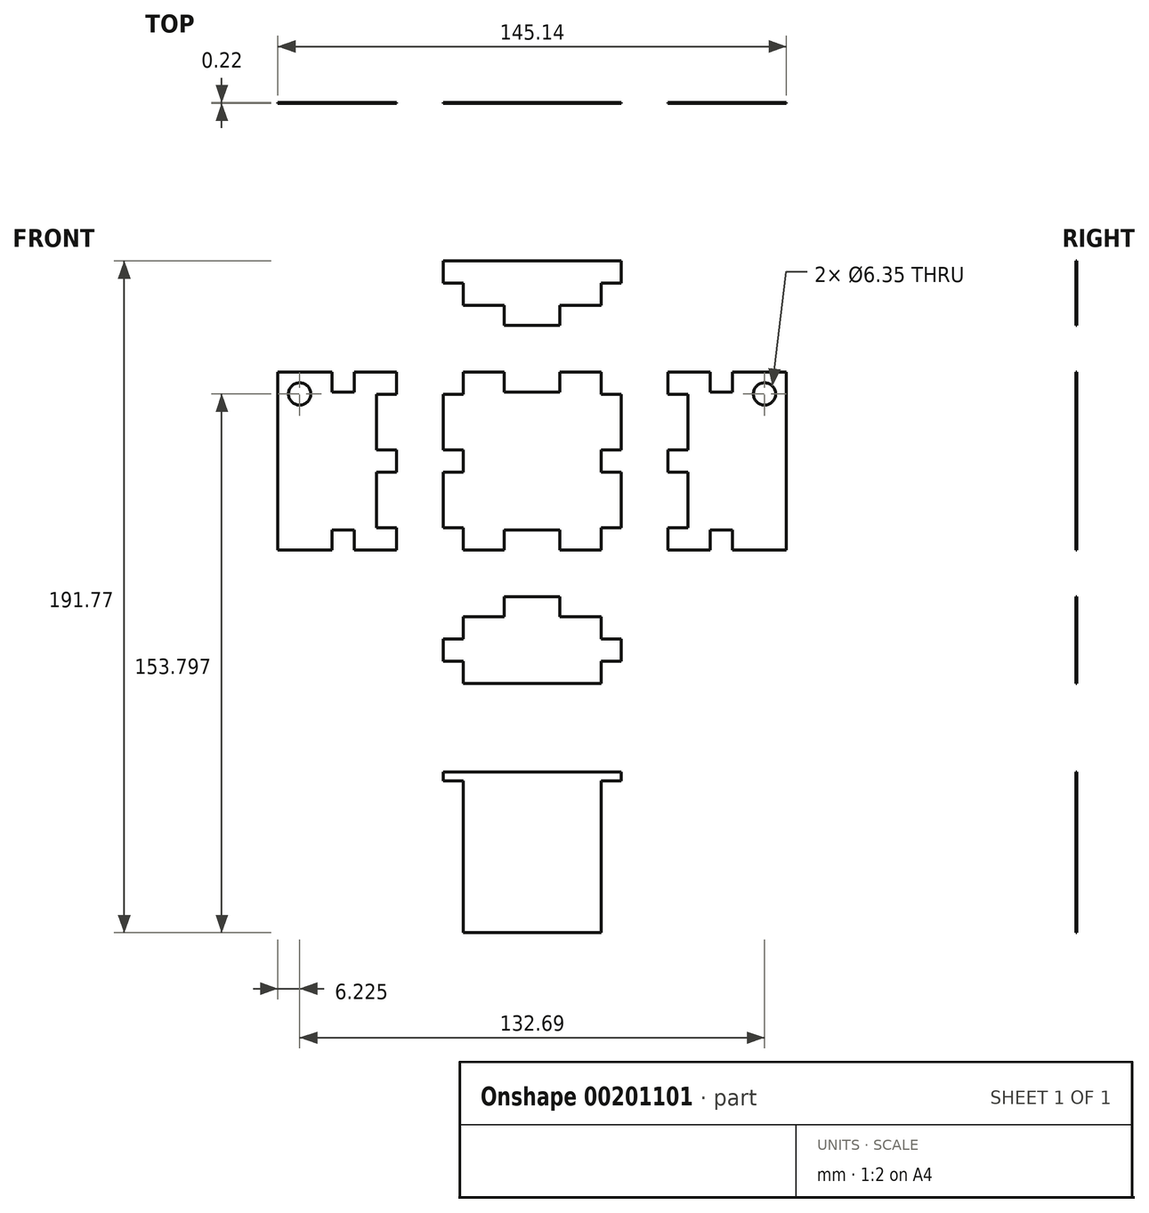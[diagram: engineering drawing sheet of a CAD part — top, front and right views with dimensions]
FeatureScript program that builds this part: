
annotation { "Feature Type Name" : "Feature", "Feature Type Description" : "" }
export const myFeature = defineFeature(function(context is Context, id is Id, definition is map)
    precondition{}
    {
        {
            assignVariable(context, id + "F0", {"name" : "thick", "anyValue" : .224});
        }
        {
            var Q0;
            Q0=qCreatedBy(makeId("Front.planeOp"),FACE);
            var sketch = newSketch(context, id + "F1", { "sketchPlane" : qUnion([Q0])});
            skLineSegment(sketch, "E0.bottom", {"start": v(-19.71, 25.4) * mm, "end": v(-7.94, 25.4) * mm});
            skLineSegment(sketch, "E0.top", {"start": v(-19.71, -25.4) * mm, "end": v(-7.94, -25.4) * mm});
            skLineSegment(sketch, "E0.left", {"start": v(-25.4, 19.05) * mm, "end": v(-25.4, 3.17) * mm});
            skLineSegment(sketch, "E0.right", {"start": v(25.4, 19.05) * mm, "end": v(25.4, 3.17) * mm});
            skPoint(sketch, "E0.middle", {"position": v(0, 0) * mm});
            skLineSegment(sketch, "E1.bottom", {"start": v(-44.45, 25.4) * mm, "end": v(-50.8, 25.4) * mm});
            skLineSegment(sketch, "E1.top", {"start": v(-44.45, -25.4) * mm, "end": v(-50.8, -25.4) * mm});
            skLineSegment(sketch, "E1.left", {"start": v(-44.45, 19.05) * mm, "end": v(-44.45, 3.17) * mm});
            skLineSegment(sketch, "E1.right", {"start": v(-63.5, 12.95) * mm, "end": v(-63.5, -25.4) * mm});
            skLineSegment(sketch, "E2.bottom", {"start": v(25.4, 44.45) * mm, "end": v(7.94, 44.45) * mm});
            skLineSegment(sketch, "E2.top", {"start": v(25.4, 57.15) * mm, "end": v(-25.4, 57.15) * mm});
            skLineSegment(sketch, "E2.left", {"start": v(25.4, 44.45) * mm, "end": v(25.4, 57.15) * mm, "construction": true});
            skLineSegment(sketch, "E2.right", {"start": v(-25.4, 44.45) * mm, "end": v(-25.4, 57.15) * mm, "construction": true});
            skCircle(sketch, "E3", {"center": v(-66.34, 19.18) * mm, "radius": 3.18 * mm});
            skArc(sketch, "E4", {"start": v(-66.34, 25.4) * mm, "mid": v(-72.57, 19.18) * mm, "end": v(-66.34, 12.95) * mm});
            skLineSegment(sketch, "E5", {"start": v(-63.5, 25.4) * mm, "end": v(-66.34, 25.4) * mm});
            skLineSegment(sketch, "E6", {"start": v(-66.34, 12.95) * mm, "end": v(-63.5, 12.95) * mm});
            skLineSegment(sketch, "E7", {"start": v(0, 25.4) * mm, "end": v(0, -25.4) * mm, "construction": true});
            skLineSegment(sketch, "E8.MirrorCS", {"start": v(63.5, 25.4) * mm, "end": v(66.34, 25.4) * mm});
            skCircle(sketch, "E9.MirrorC", {"center": v(66.34, 19.18) * mm, "radius": 3.18 * mm});
            skLineSegment(sketch, "E10.MirrorCS", {"start": v(66.34, 12.95) * mm, "end": v(63.5, 12.95) * mm});
            skLineSegment(sketch, "E11.MirrorCS", {"start": v(63.5, 12.95) * mm, "end": v(63.5, -25.4) * mm});
            skLineSegment(sketch, "E12.MirrorCS", {"start": v(44.45, 19.05) * mm, "end": v(44.45, 3.17) * mm});
            skLineSegment(sketch, "E13.MirrorCS", {"start": v(44.45, -25.4) * mm, "end": v(50.8, -25.4) * mm});
            skLineSegment(sketch, "E14.MirrorCS", {"start": v(44.45, 25.4) * mm, "end": v(63.5, 25.4) * mm});
            skArc(sketch, "E15.MirrorCS", {"start": v(66.34, 25.4) * mm, "mid": v(72.57, 19.18) * mm, "end": v(66.34, 12.95) * mm});
            skLineSegment(sketch, "E16.bottom", {"start": v(-25.4, -44.45) * mm, "end": v(-7.94, -44.45) * mm});
            skLineSegment(sketch, "E16.top", {"start": v(-25.4, -63.5) * mm, "end": v(25.4, -63.5) * mm});
            skLineSegment(sketch, "E16.left", {"start": v(-25.4, -44.45) * mm, "end": v(-25.4, -63.5) * mm, "construction": true});
            skLineSegment(sketch, "E16.right", {"start": v(25.4, -44.45) * mm, "end": v(25.4, -63.5) * mm, "construction": true});
            skLineSegment(sketch, "E17.bottom", {"start": v(-19.71, -82.55) * mm, "end": v(19.71, -82.55) * mm});
            skLineSegment(sketch, "E17.top", {"start": v(-19.71, -92.71) * mm, "end": v(19.71, -92.71) * mm, "construction": true});
            skLineSegment(sketch, "E17.left", {"start": v(-19.71, -82.55) * mm, "end": v(-19.71, -88.77) * mm});
            skLineSegment(sketch, "E17.right", {"start": v(19.71, -82.55) * mm, "end": v(19.71, -88.77) * mm});
            skLineSegment(sketch, "E18", {"start": v(-19.71, 25.4) * mm, "end": v(-19.71, 19.05) * mm});
            skLineSegment(sketch, "E19", {"start": v(-19.71, 19.05) * mm, "end": v(-25.4, 19.05) * mm});
            skLineSegment(sketch, "E20", {"start": v(-25.4, 3.17) * mm, "end": v(-19.71, 3.17) * mm});
            skLineSegment(sketch, "E21", {"start": v(-19.71, 3.17) * mm, "end": v(-19.71, -3.18) * mm});
            skLineSegment(sketch, "E22", {"start": v(-19.71, -3.18) * mm, "end": v(-25.4, -3.18) * mm});
            skLineSegment(sketch, "E23", {"start": v(-25.4, -19.05) * mm, "end": v(-19.71, -19.05) * mm});
            skLineSegment(sketch, "E24", {"start": v(-19.71, -19.05) * mm, "end": v(-19.71, -25.4) * mm});
            skLineSegment(sketch, "E25", {"start": v(-44.45, 25.4) * mm, "end": v(-38.76, 25.4) * mm});
            skLineSegment(sketch, "E26", {"start": v(-38.76, 25.4) * mm, "end": v(-38.76, 19.05) * mm});
            skLineSegment(sketch, "E27", {"start": v(-38.76, 19.05) * mm, "end": v(-44.45, 19.05) * mm});
            skLineSegment(sketch, "E28", {"start": v(-44.45, 3.17) * mm, "end": v(-38.76, 3.17) * mm});
            skLineSegment(sketch, "E29", {"start": v(-38.76, 3.17) * mm, "end": v(-38.76, -3.18) * mm});
            skLineSegment(sketch, "E30", {"start": v(-38.76, -3.18) * mm, "end": v(-44.45, -3.18) * mm});
            skLineSegment(sketch, "E31", {"start": v(-44.45, -19.05) * mm, "end": v(-38.76, -19.05) * mm});
            skLineSegment(sketch, "E32", {"start": v(-38.76, -19.05) * mm, "end": v(-38.76, -25.4) * mm});
            skLineSegment(sketch, "E33", {"start": v(-38.76, -25.4) * mm, "end": v(-44.45, -25.4) * mm});
            skLineSegment(sketch, "E34.MirrorCS", {"start": v(38.76, 19.05) * mm, "end": v(44.45, 19.05) * mm});
            skLineSegment(sketch, "E35.MirrorCS", {"start": v(38.76, 25.4) * mm, "end": v(38.76, 19.05) * mm});
            skLineSegment(sketch, "E36.MirrorCS", {"start": v(44.45, 3.17) * mm, "end": v(38.76, 3.17) * mm});
            skLineSegment(sketch, "E37.MirrorCS", {"start": v(44.45, 25.4) * mm, "end": v(38.76, 25.4) * mm});
            skLineSegment(sketch, "E38.MirrorCS", {"start": v(38.76, 3.17) * mm, "end": v(38.76, -3.18) * mm});
            skLineSegment(sketch, "E39.MirrorCS", {"start": v(38.76, -3.18) * mm, "end": v(44.45, -3.18) * mm});
            skLineSegment(sketch, "E40.MirrorCS", {"start": v(38.76, -19.05) * mm, "end": v(38.76, -25.4) * mm});
            skLineSegment(sketch, "E41.MirrorCS", {"start": v(38.76, -25.4) * mm, "end": v(44.45, -25.4) * mm});
            skLineSegment(sketch, "E42.MirrorCS", {"start": v(44.45, -19.05) * mm, "end": v(38.76, -19.05) * mm});
            skLineSegment(sketch, "E43.MirrorCS", {"start": v(19.71, 19.05) * mm, "end": v(25.4, 19.05) * mm});
            skLineSegment(sketch, "E44.MirrorCS", {"start": v(19.71, 25.4) * mm, "end": v(19.71, 19.05) * mm});
            skLineSegment(sketch, "E45.MirrorCS", {"start": v(25.4, 3.17) * mm, "end": v(19.71, 3.17) * mm});
            skLineSegment(sketch, "E46.MirrorCS", {"start": v(19.71, 3.17) * mm, "end": v(19.71, -3.18) * mm});
            skLineSegment(sketch, "E47.MirrorCS", {"start": v(19.71, -3.18) * mm, "end": v(25.4, -3.18) * mm});
            skLineSegment(sketch, "E48.MirrorCS", {"start": v(25.4, -19.05) * mm, "end": v(19.71, -19.05) * mm});
            skLineSegment(sketch, "E49.MirrorCS", {"start": v(19.71, -19.05) * mm, "end": v(19.71, -25.4) * mm});
            skLineSegment(sketch, "E50", {"start": v(-7.94, 25.4) * mm, "end": v(-7.94, 19.71) * mm});
            skLineSegment(sketch, "E51", {"start": v(-7.94, 19.71) * mm, "end": v(7.94, 19.71) * mm});
            skLineSegment(sketch, "E52", {"start": v(7.94, 19.71) * mm, "end": v(7.94, 25.4) * mm});
            skPoint(sketch, "E53", {"position": v(0, 19.71) * mm});
            skLineSegment(sketch, "E54", {"start": v(-25.4, 0) * mm, "end": v(25.4, 0) * mm, "construction": true});
            skLineSegment(sketch, "E55.MirrorCS", {"start": v(7.94, -19.71) * mm, "end": v(7.94, -25.4) * mm});
            skLineSegment(sketch, "E56.MirrorCS", {"start": v(-7.94, -19.71) * mm, "end": v(7.94, -19.71) * mm});
            skLineSegment(sketch, "E57.MirrorCS", {"start": v(-7.94, -25.4) * mm, "end": v(-7.94, -19.71) * mm});
            skPoint(sketch, "E58.MirrorP", {"position": v(0, -19.71) * mm});
            skLineSegment(sketch, "E59", {"start": v(-53.97, 25.4) * mm, "end": v(-53.97, 19.71) * mm, "construction": true});
            skLineSegment(sketch, "E60", {"start": v(-53.97, 19.71) * mm, "end": v(-57.15, 19.71) * mm, "construction": true});
            skLineSegment(sketch, "E61", {"start": v(-57.15, 19.71) * mm, "end": v(-57.15, 25.4) * mm});
            skLineSegment(sketch, "E62", {"start": v(-57.15, 19.71) * mm, "end": v(-50.8, 19.71) * mm});
            skLineSegment(sketch, "E63", {"start": v(-50.8, 19.71) * mm, "end": v(-50.8, 25.4) * mm});
            skLineSegment(sketch, "E64", {"start": v(-25.4, 50.8) * mm, "end": v(-31.09, 50.8) * mm, "construction": true});
            skPoint(sketch, "E64.endSnap0", {"position": v(-25.4, 50.8) * mm});
            skLineSegment(sketch, "E65", {"start": v(-31.09, 50.8) * mm, "end": v(-31.09, 57.15) * mm, "construction": true});
            skLineSegment(sketch, "E66", {"start": v(-31.09, 57.15) * mm, "end": v(-25.4, 57.15) * mm, "construction": true});
            skLineSegment(sketch, "E67.MirrorCS", {"start": v(53.97, 19.71) * mm, "end": v(57.15, 19.71) * mm, "construction": true});
            skLineSegment(sketch, "E68.MirrorCS", {"start": v(57.15, 19.71) * mm, "end": v(50.8, 19.71) * mm});
            skLineSegment(sketch, "E69.MirrorCS", {"start": v(57.15, 19.71) * mm, "end": v(57.15, 25.4) * mm});
            skLineSegment(sketch, "E70.MirrorCS", {"start": v(53.97, 25.4) * mm, "end": v(53.97, 19.71) * mm, "construction": true});
            skLineSegment(sketch, "E71.MirrorCS", {"start": v(50.8, 19.71) * mm, "end": v(50.8, 25.4) * mm});
            skPoint(sketch, "E72.MirrorP", {"position": v(25.4, 50.8) * mm});
            skLineSegment(sketch, "E73.MirrorCS", {"start": v(31.09, 57.15) * mm, "end": v(25.4, 57.15) * mm, "construction": true});
            skLineSegment(sketch, "E74.MirrorCS", {"start": v(25.4, 50.8) * mm, "end": v(31.09, 50.8) * mm, "construction": true});
            skLineSegment(sketch, "E75.MirrorCS", {"start": v(31.09, 50.8) * mm, "end": v(31.09, 57.15) * mm, "construction": true});
            skPoint(sketch, "E76.MirrorP", {"position": v(-25.4, -50.8) * mm});
            skLineSegment(sketch, "E77.MirrorCS", {"start": v(-25.4, -50.8) * mm, "end": v(-31.09, -50.8) * mm, "construction": true});
            skLineSegment(sketch, "E78.MirrorCS", {"start": v(-31.09, -57.15) * mm, "end": v(-25.4, -57.15) * mm, "construction": true});
            skLineSegment(sketch, "E79.MirrorCS", {"start": v(-31.09, -50.8) * mm, "end": v(-31.09, -57.15) * mm, "construction": true});
            skPoint(sketch, "E80.MirrorP", {"position": v(25.4, -50.8) * mm});
            skLineSegment(sketch, "E81.MirrorCS", {"start": v(25.4, -50.8) * mm, "end": v(31.09, -50.8) * mm, "construction": true});
            skLineSegment(sketch, "E82.MirrorCS", {"start": v(31.09, -50.8) * mm, "end": v(31.09, -57.15) * mm, "construction": true});
            skLineSegment(sketch, "E83.MirrorCS", {"start": v(31.09, -57.15) * mm, "end": v(25.4, -57.15) * mm, "construction": true});
            skLineSegment(sketch, "E84.MirrorCS", {"start": v(50.8, -19.71) * mm, "end": v(50.8, -25.4) * mm});
            skLineSegment(sketch, "E85.MirrorCS", {"start": v(57.15, -19.71) * mm, "end": v(50.8, -19.71) * mm});
            skLineSegment(sketch, "E86.MirrorCS", {"start": v(57.15, -19.71) * mm, "end": v(57.15, -25.4) * mm});
            skLineSegment(sketch, "E87.MirrorCS", {"start": v(-57.15, -19.71) * mm, "end": v(-57.15, -25.4) * mm});
            skLineSegment(sketch, "E88.MirrorCS", {"start": v(-57.15, -19.71) * mm, "end": v(-50.8, -19.71) * mm});
            skLineSegment(sketch, "E89.MirrorCS", {"start": v(-50.8, -19.71) * mm, "end": v(-50.8, -25.4) * mm});
            skLineSegment(sketch, "E90", {"start": v(-25.4, -102.87) * mm, "end": v(-25.4, -134.62) * mm});
            skLineSegment(sketch, "E91", {"start": v(-25.4, -134.62) * mm, "end": v(25.4, -134.62) * mm});
            skLineSegment(sketch, "E92", {"start": v(25.4, -134.62) * mm, "end": v(25.4, -102.87) * mm});
            skLineSegment(sketch, "E93", {"start": v(-19.71, -88.77) * mm, "end": v(-25.4, -88.77) * mm});
            skLineSegment(sketch, "E94", {"start": v(-25.4, -88.77) * mm, "end": v(-25.4, -91.31) * mm});
            skLineSegment(sketch, "E95", {"start": v(-25.4, -91.31) * mm, "end": v(-19.71, -91.31) * mm});
            skLineSegment(sketch, "E96", {"start": v(-19.71, -92.71) * mm, "end": v(-19.71, -96.77) * mm});
            skLineSegment(sketch, "E97", {"start": v(-19.71, -96.77) * mm, "end": v(-25.4, -102.87) * mm});
            skLineSegment(sketch, "E98.MirrorCS", {"start": v(19.71, -92.71) * mm, "end": v(19.71, -96.77) * mm});
            skLineSegment(sketch, "E99.MirrorCS", {"start": v(19.71, -96.77) * mm, "end": v(25.4, -102.87) * mm});
            skLineSegment(sketch, "E100.MirrorCS", {"start": v(25.4, -88.77) * mm, "end": v(25.4, -91.31) * mm});
            skLineSegment(sketch, "E101.MirrorCS", {"start": v(25.4, -91.31) * mm, "end": v(19.71, -91.31) * mm});
            skLineSegment(sketch, "E102.MirrorCS", {"start": v(19.71, -88.77) * mm, "end": v(25.4, -88.77) * mm});
            skLineSegment(sketch, "E103", {"start": v(-7.94, 44.45) * mm, "end": v(-7.94, 38.76) * mm});
            skLineSegment(sketch, "E104", {"start": v(-7.94, 38.76) * mm, "end": v(7.94, 38.76) * mm});
            skLineSegment(sketch, "E105", {"start": v(7.94, 38.76) * mm, "end": v(7.94, 44.45) * mm});
            skLineSegment(sketch, "E106", {"start": v(-7.94, -44.45) * mm, "end": v(-7.94, -38.76) * mm});
            skLineSegment(sketch, "E107", {"start": v(-7.94, -38.76) * mm, "end": v(7.94, -38.76) * mm});
            skLineSegment(sketch, "E108", {"start": v(7.94, -38.76) * mm, "end": v(7.94, -44.45) * mm});
            skLineSegment(sketch, "E109", {"start": v(-19.71, 44.45) * mm, "end": v(-19.71, 50.8) * mm});
            skLineSegment(sketch, "E110", {"start": v(19.71, 44.45) * mm, "end": v(19.71, 50.8) * mm});
            skLineSegment(sketch, "E111", {"start": v(-19.71, 50.8) * mm, "end": v(-25.4, 50.8) * mm});
            skLineSegment(sketch, "E112", {"start": v(-25.4, 50.8) * mm, "end": v(-25.4, 57.15) * mm});
            skLineSegment(sketch, "E113", {"start": v(25.4, 57.15) * mm, "end": v(25.4, 50.8) * mm});
            skLineSegment(sketch, "E114", {"start": v(19.71, 50.8) * mm, "end": v(25.4, 50.8) * mm});
            skLineSegment(sketch, "E115", {"start": v(-19.71, -44.45) * mm, "end": v(-19.71, -50.8) * mm});
            skLineSegment(sketch, "E116", {"start": v(19.71, -44.45) * mm, "end": v(19.71, -50.8) * mm});
            skLineSegment(sketch, "E117", {"start": v(-19.71, -50.8) * mm, "end": v(-25.4, -50.8) * mm});
            skLineSegment(sketch, "E118", {"start": v(-25.4, -57.15) * mm, "end": v(-25.4, -50.8) * mm});
            skLineSegment(sketch, "E119", {"start": v(-25.4, -57.15) * mm, "end": v(-19.71, -57.15) * mm});
            skLineSegment(sketch, "E120", {"start": v(25.4, -50.8) * mm, "end": v(19.71, -50.8) * mm});
            skLineSegment(sketch, "E121", {"start": v(25.4, -50.8) * mm, "end": v(25.4, -57.15) * mm});
            skLineSegment(sketch, "E122", {"start": v(25.4, -57.15) * mm, "end": v(19.71, -57.15) * mm});
            skPoint(sketch, "E123", {"position": v(25.4, -90.04) * mm});
            skPoint(sketch, "E124.orphan", {"position": v(-19.71, 57.15) * mm});
            skLineSegment(sketch, "E125.trimOffspring", {"start": v(-7.94, 44.45) * mm, "end": v(-25.4, 44.45) * mm});
            skPoint(sketch, "E126.orphan", {"position": v(19.71, 57.15) * mm});
            skLineSegment(sketch, "E127.trimOffspring", {"start": v(44.45, -3.18) * mm, "end": v(44.45, -19.05) * mm});
            skLineSegment(sketch, "E128.trimOffspring", {"start": v(57.15, -25.4) * mm, "end": v(63.5, -25.4) * mm});
            skPoint(sketch, "E129.orphan", {"position": v(25.4, -25.4) * mm});
            skLineSegment(sketch, "E130.trimOffspring", {"start": v(25.4, -3.18) * mm, "end": v(25.4, -19.05) * mm});
            skPoint(sketch, "E131.orphan", {"position": v(25.4, 25.4) * mm});
            skLineSegment(sketch, "E132.trimOffspring", {"start": v(7.94, 25.4) * mm, "end": v(19.71, 25.4) * mm});
            skPoint(sketch, "E133.orphan", {"position": v(-25.4, 25.4) * mm});
            skLineSegment(sketch, "E134.trimOffspring", {"start": v(-53.97, 25.4) * mm, "end": v(-63.5, 25.4) * mm});
            skLineSegment(sketch, "E135.trimOffspring", {"start": v(-44.45, -3.18) * mm, "end": v(-44.45, -19.05) * mm});
            skLineSegment(sketch, "E136.trimOffspring", {"start": v(-25.4, -3.18) * mm, "end": v(-25.4, -19.05) * mm});
            skLineSegment(sketch, "E137.trimOffspring", {"start": v(-57.15, -25.4) * mm, "end": v(-63.5, -25.4) * mm});
            skPoint(sketch, "E138.orphan", {"position": v(-25.4, -25.4) * mm});
            skLineSegment(sketch, "E139.trimOffspring", {"start": v(7.94, -25.4) * mm, "end": v(19.71, -25.4) * mm});
            skLineSegment(sketch, "E140.trimOffspring", {"start": v(19.71, -57.15) * mm, "end": v(19.71, -63.5) * mm});
            skLineSegment(sketch, "E141.trimOffspring", {"start": v(7.94, -44.45) * mm, "end": v(25.4, -44.45) * mm});
            skLineSegment(sketch, "E142.trimOffspring", {"start": v(-19.71, -57.15) * mm, "end": v(-19.71, -63.5) * mm});
            skLineSegment(sketch, "E143.trimOffspring", {"start": v(19.71, -91.31) * mm, "end": v(19.71, -92.71) * mm});
            skLineSegment(sketch, "E144.trimOffspring", {"start": v(-19.71, -91.31) * mm, "end": v(-19.71, -92.71) * mm});
            skLineSegment(sketch, "E145.bottom", {"start": v(-75.63, 66.18) * mm, "end": v(74.77, 66.18) * mm});
            skLineSegment(sketch, "E145.top", {"start": v(-75.63, -141.7) * mm, "end": v(74.77, -141.7) * mm});
            skLineSegment(sketch, "E145.left", {"start": v(-75.63, 66.18) * mm, "end": v(-75.63, -141.7) * mm});
            skLineSegment(sketch, "E145.right", {"start": v(74.77, 66.18) * mm, "end": v(74.77, -141.7) * mm});
            skLineSegment(sketch, "E146", {"start": v(-19.71, -96.77) * mm, "end": v(-19.71, -134.62) * mm});
            skLineSegment(sketch, "E147", {"start": v(19.71, -96.77) * mm, "end": v(19.71, -134.62) * mm});
            skLineSegment(sketch, "E148", {"start": v(-66.34, 25.4) * mm, "end": v(-72.57, 25.4) * mm});
            skPoint(sketch, "E148.endSnap0", {"position": v(-72.57, 19.18) * mm});
            skLineSegment(sketch, "E149", {"start": v(-72.57, 25.4) * mm, "end": v(-72.57, -25.4) * mm});
            skLineSegment(sketch, "E150", {"start": v(-72.57, -25.4) * mm, "end": v(-63.5, -25.4) * mm});
            skLineSegment(sketch, "E151", {"start": v(66.34, 25.4) * mm, "end": v(72.57, 25.4) * mm});
            skPoint(sketch, "E151.endSnap0", {"position": v(72.57, 19.18) * mm});
            skLineSegment(sketch, "E152", {"start": v(72.57, 25.4) * mm, "end": v(72.57, -25.4) * mm});
            skLineSegment(sketch, "E153", {"start": v(72.57, -25.4) * mm, "end": v(63.5, -25.4) * mm});
            skLineSegment(sketch, "E154", {"start": v(-19.71, -88.77) * mm, "end": v(19.71, -88.77) * mm});
            skSolve(sketch);
        }
        {
            var Q0;
            {var subQ3=sQuery(id+"F1.wireOp",EDGE,"E2.bottom");Q0=makeQuery(id+"F1.imprint","IMPRINT",FACE,{"disambiguationData":[TD([[makeQuery(id+"F1.imprint","IMPRINT",EDGE,{"derivedFrom":subQ3}),-1.0]])]});}
            var Q1;
            {var subQ2=sQuery(id+"F1.wireOp",EDGE,"E64");Q1=makeQuery(id+"F1.imprint","IMPRINT",FACE,{"disambiguationData":[TD([[makeQuery(id+"F1.imprint","IMPRINT",EDGE,{"derivedFrom":subQ2}),-1.0]])]});}
            var Q2;
            {var subQ0=sQuery(id+"F1.wireOp",EDGE,"E73.MirrorCS");Q2=makeQuery(id+"F1.imprint","IMPRINT",FACE,{"disambiguationData":[TD([[makeQuery(id+"F1.imprint","IMPRINT",EDGE,{"derivedFrom":subQ0}),1.0]])]});}
            var Q3;
            {var subQ0=sQuery(id+"F1.wireOp",EDGE,"E1.right");Q3=makeQuery(id+"F1.imprint","IMPRINT",FACE,{"disambiguationData":[TD([[makeQuery(id+"F1.imprint","IMPRINT",EDGE,{"derivedFrom":subQ0}),1.0]])]});}
            var Q4;
            {var subQ0=sQuery(id+"F1.wireOp",EDGE,"E25");Q4=makeQuery(id+"F1.imprint","IMPRINT",FACE,{"disambiguationData":[TD([[makeQuery(id+"F1.imprint","IMPRINT",EDGE,{"derivedFrom":subQ0}),-1.0]])]});}
            var Q5;
            {var subQ0=sQuery(id+"F1.wireOp",EDGE,"E28");Q5=makeQuery(id+"F1.imprint","IMPRINT",FACE,{"disambiguationData":[TD([[makeQuery(id+"F1.imprint","IMPRINT",EDGE,{"derivedFrom":subQ0}),-1.0]])]});}
            var Q6;
            {var subQ2=sQuery(id+"F1.wireOp",EDGE,"E31");Q6=makeQuery(id+"F1.imprint","IMPRINT",FACE,{"disambiguationData":[TD([[makeQuery(id+"F1.imprint","IMPRINT",EDGE,{"derivedFrom":subQ2}),-1.0]])]});}
            var Q7;
            {var subQ18=sQuery(id+"F1.wireOp",EDGE,"E18");Q7=makeQuery(id+"F1.imprint","IMPRINT",FACE,{"disambiguationData":[TD([[makeQuery(id+"F1.imprint","IMPRINT",EDGE,{"derivedFrom":subQ18}),1.0]])]});}
            var Q8;
            {var subQ6=sQuery(id+"F1.wireOp",EDGE,"E8.MirrorCS");Q8=makeQuery(id+"F1.imprint","IMPRINT",FACE,{"disambiguationData":[TD([[makeQuery(id+"F1.imprint","IMPRINT",EDGE,{"derivedFrom":subQ6}),-1.0]])]});}
            var Q9;
            {var subQ2=sQuery(id+"F1.wireOp",EDGE,"E34.MirrorCS");Q9=makeQuery(id+"F1.imprint","IMPRINT",FACE,{"disambiguationData":[TD([[makeQuery(id+"F1.imprint","IMPRINT",EDGE,{"derivedFrom":subQ2}),1.0]])]});}
            var Q10;
            {var subQ0=sQuery(id+"F1.wireOp",EDGE,"E36.MirrorCS");Q10=makeQuery(id+"F1.imprint","IMPRINT",FACE,{"disambiguationData":[TD([[makeQuery(id+"F1.imprint","IMPRINT",EDGE,{"derivedFrom":subQ0}),1.0]])]});}
            var Q11;
            Q11=makeQuery(id+"F1.imprint","IMPRINT",FACE,{"disambiguationData":[TD([[makeQuery(id+"F1.imprint","IMPRINT",EDGE,{"derivedFrom":sQuery(id+"F1.wireOp",EDGE,"E40.MirrorCS")}),1.0]])]});
            var Q12;
            {var subQ0=sQuery(id+"F1.wireOp",EDGE,"E77.MirrorCS");Q12=makeQuery(id+"F1.imprint","IMPRINT",FACE,{"disambiguationData":[TD([[makeQuery(id+"F1.imprint","IMPRINT",EDGE,{"derivedFrom":subQ0}),1.0]])]});}
            var Q13;
            {var subQ3=sQuery(id+"F1.wireOp",EDGE,"E16.bottom");Q13=makeQuery(id+"F1.imprint","IMPRINT",FACE,{"disambiguationData":[TD([[makeQuery(id+"F1.imprint","IMPRINT",EDGE,{"derivedFrom":subQ3}),-1.0]])]});}
            var Q14;
            {var subQ0=sQuery(id+"F1.wireOp",EDGE,"E81.MirrorCS");Q14=makeQuery(id+"F1.imprint","IMPRINT",FACE,{"disambiguationData":[TD([[makeQuery(id+"F1.imprint","IMPRINT",EDGE,{"derivedFrom":subQ0}),-1.0]])]});}
            var Q15;
            {var subQ0=sQuery(id+"F1.wireOp",EDGE,"E93");Q15=makeQuery(id+"F1.imprint","IMPRINT",FACE,{"disambiguationData":[TD([[makeQuery(id+"F1.imprint","IMPRINT",EDGE,{"derivedFrom":subQ0}),1.0]])]});}
            var Q16;
            Q16=makeQuery(id+"F1.imprint","IMPRINT",FACE,{"disambiguationData":[TD([[makeQuery(id+"F1.imprint","IMPRINT",EDGE,{"derivedFrom":sQuery(id+"F1.wireOp",EDGE,"E100.MirrorCS")}),-1.0]])]});
            var Q17;
            {var subQ0=sQuery(id+"F1.wireOp",EDGE,"E103");Q17=makeQuery(id+"F1.imprint","IMPRINT",FACE,{"disambiguationData":[TD([[makeQuery(id+"F1.imprint","IMPRINT",EDGE,{"derivedFrom":subQ0}),1.0]])]});}
            var Q18;
            {var subQ0=sQuery(id+"F1.wireOp",EDGE,"E106");Q18=makeQuery(id+"F1.imprint","IMPRINT",FACE,{"disambiguationData":[TD([[makeQuery(id+"F1.imprint","IMPRINT",EDGE,{"derivedFrom":subQ0}),-1.0]])]});}
            var Q19;
            {var subQ0=sQuery(id+"F1.wireOp",EDGE,"E117");Q19=makeQuery(id+"F1.imprint","IMPRINT",FACE,{"disambiguationData":[TD([[makeQuery(id+"F1.imprint","IMPRINT",EDGE,{"derivedFrom":subQ0}),1.0]])]});}
            var Q20;
            {var subQ0=sQuery(id+"F1.wireOp",EDGE,"E120");Q20=makeQuery(id+"F1.imprint","IMPRINT",FACE,{"disambiguationData":[TD([[makeQuery(id+"F1.imprint","IMPRINT",EDGE,{"derivedFrom":subQ0}),1.0]])]});}
            var Q21;
            {var subQ4=sQuery(id+"F1.wireOp",EDGE,"E111");Q21=makeQuery(id+"F1.imprint","IMPRINT",FACE,{"disambiguationData":[TD([[makeQuery(id+"F1.imprint","IMPRINT",EDGE,{"derivedFrom":subQ4}),-1.0]])]});}
            var Q22;
            {var subQ0=sQuery(id+"F1.wireOp",EDGE,"E113");Q22=makeQuery(id+"F1.imprint","IMPRINT",FACE,{"disambiguationData":[TD([[makeQuery(id+"F1.imprint","IMPRINT",EDGE,{"derivedFrom":subQ0}),-1.0]])]});}
            var Q23;
            Q23=makeQuery(id+"F1.imprint","IMPRINT",FACE,{"disambiguationData":[TD([[makeQuery(id+"F1.imprint","IMPRINT",EDGE,{"derivedFrom":sQuery(id+"F1.wireOp",EDGE,"E1.right")}),-1.0]])]});
            var Q24;
            {var subQ0=sQuery(id+"F1.wireOp",EDGE,"E151");Q24=makeQuery(id+"F1.imprint","IMPRINT",FACE,{"disambiguationData":[TD([[makeQuery(id+"F1.imprint","IMPRINT",EDGE,{"derivedFrom":subQ0}),-1.0]])]});}
            var Q25;
            {var subQ1=sQuery(id+"F1.wireOp",EDGE,"E10.MirrorCS");Q25=makeQuery(id+"F1.imprint","IMPRINT",FACE,{"disambiguationData":[TD([[makeQuery(id+"F1.imprint","IMPRINT",EDGE,{"derivedFrom":subQ1}),1.0]])]});}
            var Q26;
            {var subQ0=sQuery(id+"F1.wireOp",EDGE,"E148");Q26=makeQuery(id+"F1.imprint","IMPRINT",FACE,{"disambiguationData":[TD([[makeQuery(id+"F1.imprint","IMPRINT",EDGE,{"derivedFrom":subQ0}),1.0]])]});}
            extrude(context, id + "F2", {"entities" : qUnion([Q0, Q1, Q2, Q3, Q4, Q5, Q6, Q7, Q8, Q9, Q10, Q11, Q12, Q13, Q14, Q15, Q16, Q17, Q18, Q19, Q20, Q21, Q22, Q23, Q24, Q25, Q26]), "depth" : (getVariable(context, 'thick')) * mm});
        }
    });
